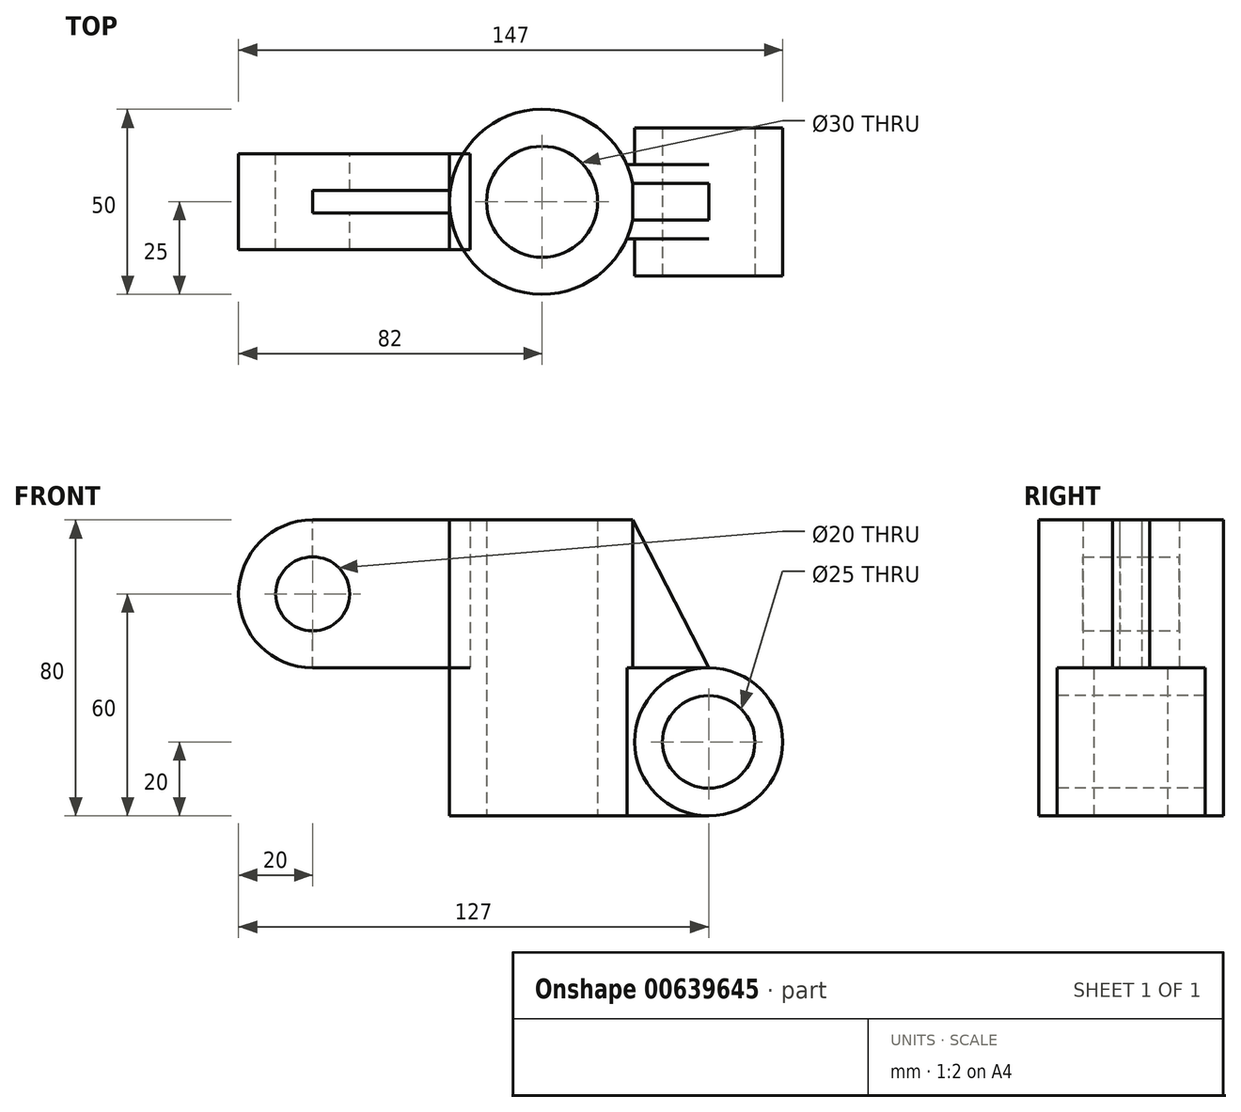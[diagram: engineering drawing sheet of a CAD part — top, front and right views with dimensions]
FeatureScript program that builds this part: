
annotation { "Feature Type Name" : "Feature", "Feature Type Description" : "" }
export const myFeature = defineFeature(function(context is Context, id is Id, definition is map)
    precondition{}
    {
        {
            var Q0;
            Q0=qCreatedBy(makeId("Top.planeOp"),FACE);
            var sketch = newSketch(context, id + "F0", { "sketchPlane" : qUnion([Q0])});
            skCircle(sketch, "E0", {"center": v(0, 0) * mm, "radius": 25 * mm});
            skCircle(sketch, "E1", {"center": v(0, 0) * mm, "radius": 15 * mm});
            skSolve(sketch);
        }
        {
            var Q0;
            Q0 = qSketchRegion(id + "F0", true);
            extrude(context, id + "F1", {"entities" : qUnion([Q0]), "depth" : 80 * mm, "offsetDistance" : 25 * mm});
        }
        {
            var Q0;
            Q0=qCreatedBy(makeId("Right.planeOp"),FACE);
            var sketch = newSketch(context, id + "F2", { "sketchPlane" : qUnion([Q0])});
            skLineSegment(sketch, "E2", {"start": v(-25, 0) * mm, "end": v(-25, 80) * mm});
            skLineSegment(sketch, "E3", {"start": v(25, 80) * mm, "end": v(25, 0) * mm});
            skLineSegment(sketch, "E4.0.0", {"start": v(-25, 80) * mm, "end": v(25, 80) * mm});
            skSolve(sketch);
        }
        {
            var Q0;
            Q0=makeQuery(id+"F1.opExtrude","CAP_FACE",FACE,{"disambiguationData":[OSD([sQuery(id+"F0.wireOp",EDGE,"E0"),sQuery(id+"F0.wireOp",EDGE,"E1")])],"isStart":false});
            var sketch = newSketch(context, id + "F3", { "sketchPlane" : qUnion([Q0])});
            skCircle(sketch, "E5.0", {"center": v(0, 0) * mm, "radius": 25 * mm});
            skPoint(sketch, "E6.0", {"position": v(0, 25) * mm});
            skLineSegment(sketch, "E7", {"start": v(0, 25) * mm, "end": v(45, 25) * mm});
            skLineSegment(sketch, "E8", {"start": v(45, 25) * mm, "end": v(45, -51.18) * mm});
            skLineSegment(sketch, "E9", {"start": v(0, 0) * mm, "end": v(45, 0) * mm});
            skLineSegment(sketch, "E10", {"start": v(45, 0) * mm, "end": v(45, 5) * mm});
            skLineSegment(sketch, "E11", {"start": v(45, 5) * mm, "end": v(45, -5) * mm});
            skLineSegment(sketch, "E12", {"start": v(45, -5) * mm, "end": v(0, -5) * mm});
            skLineSegment(sketch, "E13", {"start": v(0, -5) * mm, "end": v(0, 0) * mm});
            skLineSegment(sketch, "E14", {"start": v(0, 0) * mm, "end": v(0, 5) * mm});
            skLineSegment(sketch, "E15", {"start": v(0, 5) * mm, "end": v(45, 5) * mm});
            skSolve(sketch);
        }
        {
            var Q0;
            {var subQ0=sQuery(id+"F3.wireOp",EDGE,"E15");var subQ1=sQuery(id+"F3.wireOp",EDGE,"E5.0");var subQ2=makeQuery(id+"F3.imprint","INTERSECT",VERTEX,{"derivedFrom":[subQ1,subQ0]});Q0=makeQuery(id+"F3.imprint","IMPRINT",FACE,{"disambiguationData":[TD([[makeQuery(id+"F3.imprint","IMPRINT",EDGE,{"disambiguationData":[TD([[subQ2,1.0]])],"derivedFrom":subQ1}),-1.0]])]});}
            var Q1;
            {var subQ0=sQuery(id+"F3.wireOp",EDGE,"E12");var subQ1=sQuery(id+"F3.wireOp",EDGE,"E5.0");var subQ2=makeQuery(id+"F3.imprint","INTERSECT",VERTEX,{"derivedFrom":[subQ1,subQ0]});Q1=makeQuery(id+"F3.imprint","IMPRINT",FACE,{"disambiguationData":[TD([[makeQuery(id+"F3.imprint","IMPRINT",EDGE,{"disambiguationData":[TD([[subQ2,-1.0]])],"derivedFrom":subQ1}),-1.0]])]});}
            extrude(context, id + "F4", {"entities" : qUnion([Q0, Q1]), "operationType" : NewBodyOperationType.ADD, "oppositeDirection" : true, "depth" : 40 * mm, "offsetDistance" : 25 * mm});
        }
        {
            var Q0;
            Q0=makeQuery(id+"F4.opExtrude","SWEPT_FACE",FACE,{"disambiguationData":[OSD([sQuery(id+"F3.wireOp",EDGE,"E12")])]});
            var sketch = newSketch(context, id + "F5", { "sketchPlane" : qUnion([Q0])});
            skLineSegment(sketch, "E16", {"start": v(24.5, 80) * mm, "end": v(45, 40) * mm});
            skSolve(sketch);
        }
        {
            var Q0;
            Q0=makeQuery(id+"F5.imprint","IMPRINT",FACE,{"disambiguationData":[TD([[makeQuery(id+"F5.imprint","IMPRINT",EDGE,{"derivedFrom":sQuery(id+"F5.wireOp",EDGE,"E16")}),1.0]])]});
            extrude(context, id + "F6", {"entities" : qUnion([Q0]), "operationType" : NewBodyOperationType.REMOVE, "oppositeDirection" : true, "depth" : 25 * mm, "offsetDistance" : 25 * mm});
        }
        {
            var Q0;
            Q0=qCreatedBy(makeId("Top.planeOp"),FACE);
            var sketch = newSketch(context, id + "F7", { "sketchPlane" : qUnion([Q0])});
            skPoint(sketch, "E17.0", {"position": v(0, 0) * mm});
            skCircle(sketch, "E18.0", {"center": v(0, 0) * mm, "radius": 15 * mm});
            skCircle(sketch, "E19.0", {"center": v(0, 0) * mm, "radius": 25 * mm});
            skLineSegment(sketch, "E20", {"start": v(0, 25) * mm, "end": v(57, 25) * mm});
            skLineSegment(sketch, "E21", {"start": v(0, -25) * mm, "end": v(57, -25) * mm});
            skLineSegment(sketch, "E22", {"start": v(57, -25) * mm, "end": v(57, 25) * mm});
            skSolve(sketch);
        }
        {
            var Q0;
            Q0 = qSketchRegion(id + "F7", true);
            extrude(context, id + "F8", {"entities" : qUnion([Q0]), "operationType" : NewBodyOperationType.ADD, "depth" : 40 * mm, "offsetDistance" : 25 * mm});
        }
        {
            var Q0;
            Q0=makeQuery(id+"F8.opExtrude","CAP_FACE",FACE,{"disambiguationData":[OSD([sQuery(id+"F7.wireOp",EDGE,"E18.0"),sQuery(id+"F7.wireOp",EDGE,"E19.0"),sQuery(id+"F7.wireOp",EDGE,"E20"),sQuery(id+"F7.wireOp",EDGE,"E21"),sQuery(id+"F7.wireOp",EDGE,"E22")])],"isStart":false});
            var sketch = newSketch(context, id + "F9", { "sketchPlane" : qUnion([Q0])});
            skLineSegment(sketch, "E23", {"start": v(45, 0) * mm, "end": v(45, -10) * mm});
            skLineSegment(sketch, "E24", {"start": v(45, -10) * mm, "end": v(45, 10) * mm});
            skLineSegment(sketch, "E25", {"start": v(45, 10) * mm, "end": v(24.5, 10) * mm});
            skLineSegment(sketch, "E26", {"start": v(24.5, 10) * mm, "end": v(22.91, 10) * mm});
            skLineSegment(sketch, "E27", {"start": v(45, -10) * mm, "end": v(22.91, -10) * mm});
            skSolve(sketch);
        }
        {
            var Q0;
            {var subQ13=sQuery(id+"F9.wireOp",EDGE,"E25");Q0=makeQuery(id+"F9.imprint","IMPRINT",FACE,{"disambiguationData":[TD([[makeQuery(id+"F9.imprint","IMPRINT",EDGE,{"derivedFrom":subQ13}),-1.0]])]});}
            extrude(context, id + "F10", {"entities" : qUnion([Q0]), "operationType" : NewBodyOperationType.REMOVE, "oppositeDirection" : true, "depth" : 49.5 * mm, "offsetDistance" : 25 * mm});
        }
        {
            var Q0;
            Q0=makeQuery(id+"F10.boolean.opBoolean","COPY",FACE,{"derivedFrom":makeQuery(id+"F10.opExtrude","SWEPT_FACE",FACE,{"disambiguationData":[OSD([sQuery(id+"F9.wireOp",EDGE,"E25"),sQuery(id+"F9.wireOp",EDGE,"E26")])]})});
            var sketch = newSketch(context, id + "F11", { "sketchPlane" : qUnion([Q0])});
            skCircle(sketch, "E28", {"center": v(-45, 20) * mm, "radius": 20 * mm});
            skCircle(sketch, "E29", {"center": v(-45, 20) * mm, "radius": 12.5 * mm});
            skSolve(sketch);
        }
        {
            var Q0;
            {var subQ2=sQuery(id+"F9.wireOp",EDGE,"E25");var subQ3=makeQuery(id+"F10.boolean.opBoolean","COPY",EDGE,{"derivedFrom":makeQuery(id+"F10.opExtrude","SWEPT_EDGE",EDGE,{"disambiguationData":[OSD([sQuery(id+"F9.wireOp",EDGE,"E24"),subQ2])]})});var subQ6=sQuery(id+"F11.wireOp",EDGE,"E29");var subQ7=makeQuery(id+"F11.imprint","INTERSECT",VERTEX,{"disambiguationData":[OD(0.0)],"derivedFrom":[subQ3,subQ6]});Q0=makeQuery(id+"F11.imprint","IMPRINT",FACE,{"disambiguationData":[TD([[makeQuery(id+"F11.imprint","IMPRINT",EDGE,{"disambiguationData":[TD([[subQ7,1.0]])],"derivedFrom":subQ6}),-1.0]])]});}
            var Q1;
            {var subQ2=sQuery(id+"F9.wireOp",EDGE,"E25");var subQ3=makeQuery(id+"F10.boolean.opBoolean","COPY",EDGE,{"derivedFrom":makeQuery(id+"F10.opExtrude","SWEPT_EDGE",EDGE,{"disambiguationData":[OSD([sQuery(id+"F9.wireOp",EDGE,"E24"),subQ2])]})});var subQ6=sQuery(id+"F11.wireOp",EDGE,"E29");var subQ7=makeQuery(id+"F11.imprint","INTERSECT",VERTEX,{"disambiguationData":[OD(0.0)],"derivedFrom":[subQ3,subQ6]});Q1=makeQuery(id+"F11.imprint","IMPRINT",FACE,{"disambiguationData":[TD([[makeQuery(id+"F11.imprint","IMPRINT",EDGE,{"disambiguationData":[TD([[subQ7,-1.0]])],"derivedFrom":subQ6}),-1.0]])]});}
            extrude(context, id + "F12", {"entities" : qUnion([Q0, Q1]), "operationType" : NewBodyOperationType.ADD, "depth" : 10 * mm, "offsetDistance" : 25 * mm, "hasSecondDirection" : true, "secondDirectionOppositeDirection" : true, "secondDirectionDepth" : 30 * mm});
        }
        {
            var Q0;
            Q0=makeQuery(id+"F12.boolean.opBoolean","SPLIT",FACE,{"disambiguationData":[TD([makeQuery(id+"F10.boolean.opBoolean","COPY",FACE,{"derivedFrom":makeQuery(id+"F10.opExtrude","SWEPT_FACE",FACE,{"disambiguationData":[OSD([sQuery(id+"F9.wireOp",EDGE,"E24")])]})})])],"derivedFrom":makeQuery(id+"F10.boolean.opBoolean","COPY",FACE,{"derivedFrom":makeQuery(id+"F10.opExtrude","SWEPT_FACE",FACE,{"disambiguationData":[OSD([sQuery(id+"F9.wireOp",EDGE,"E25"),sQuery(id+"F9.wireOp",EDGE,"E26")])]})})});
            extrude(context, id + "F13", {"entities" : qUnion([Q0]), "operationType" : NewBodyOperationType.REMOVE, "oppositeDirection" : true, "depth" : 25 * mm, "offsetDistance" : 25 * mm});
        }
        {
            var Q0;
            {var subQ1=sQuery(id+"F3.wireOp",EDGE,"E5.0");var subQ8=makeQuery(id+"F3.imprint","INTERSECT",VERTEX,{"derivedFrom":[subQ1,sQuery(id+"F3.wireOp",EDGE,"E7")]});Q0=makeQuery(id+"F3.imprint","IMPRINT",FACE,{"disambiguationData":[TD([[makeQuery(id+"F3.imprint","IMPRINT",EDGE,{"disambiguationData":[TD([[subQ8,1.0]])],"derivedFrom":subQ1}),1.0]])]});}
            var sketch = newSketch(context, id + "F14", { "sketchPlane" : qUnion([Q0])});
            skArc(sketch, "E30.0.0", {"start": v(14.14, -5) * mm, "mid": v(-15, 0) * mm, "end": v(14.14, 5) * mm});
            skLineSegment(sketch, "E30.0.1", {"start": v(14.14, 5) * mm, "end": v(24.5, 5) * mm});
            skArc(sketch, "E30.0.2", {"start": v(24.5, 5) * mm, "mid": v(15.81, 19.36) * mm, "end": v(0, 25) * mm});
            skArc(sketch, "E30.0.3", {"start": v(0, 25) * mm, "mid": v(-19.36, -15.81) * mm, "end": v(24.5, -5) * mm});
            skLineSegment(sketch, "E30.0.4", {"start": v(24.5, -5) * mm, "end": v(14.14, -5) * mm});
            skLineSegment(sketch, "E31", {"start": v(0, -25) * mm, "end": v(-37, -25) * mm});
            skLineSegment(sketch, "E32", {"start": v(0, 25) * mm, "end": v(-37, 25) * mm});
            skLineSegment(sketch, "E33", {"start": v(-37, 25) * mm, "end": v(-37, -25) * mm});
            skSolve(sketch);
        }
        {
            var Q0;
            {var subQ1=sQuery(id+"F3.wireOp",EDGE,"E5.0");var subQ8=makeQuery(id+"F3.imprint","INTERSECT",VERTEX,{"derivedFrom":[subQ1,sQuery(id+"F3.wireOp",EDGE,"E7")]});Q0=makeQuery(id+"F3.imprint","IMPRINT",FACE,{"disambiguationData":[TD([[makeQuery(id+"F3.imprint","IMPRINT",EDGE,{"disambiguationData":[TD([[subQ8,1.0]])],"derivedFrom":subQ1}),1.0]])]});}
            var sketch = newSketch(context, id + "F15", { "sketchPlane" : qUnion([Q0])});
            skArc(sketch, "E34.0.0", {"start": v(14.14, -5) * mm, "mid": v(-15, 0) * mm, "end": v(14.14, 5) * mm});
            skLineSegment(sketch, "E34.0.1", {"start": v(14.14, 5) * mm, "end": v(24.5, 5) * mm});
            skArc(sketch, "E34.0.2", {"start": v(24.5, 5) * mm, "mid": v(15.81, 19.36) * mm, "end": v(0, 25) * mm});
            skArc(sketch, "E34.0.3", {"start": v(0, 25) * mm, "mid": v(-25, 0) * mm, "end": v(0, -25) * mm});
            skArc(sketch, "E34.0.4", {"start": v(0, -25) * mm, "mid": v(15.81, -19.36) * mm, "end": v(24.5, -5) * mm});
            skLineSegment(sketch, "E34.0.5", {"start": v(24.5, -5) * mm, "end": v(14.14, -5) * mm});
            skLineSegment(sketch, "E35", {"start": v(-25, 0) * mm, "end": v(-62, 0) * mm});
            skSolve(sketch);
        }
        {
            var Q0;
            Q0=qCreatedBy(makeId("Front.planeOp"),FACE);
            var sketch = newSketch(context, id + "F16", { "sketchPlane" : qUnion([Q0])});
            skLineSegment(sketch, "E36.0", {"start": v(-25, 80) * mm, "end": v(-62, 80) * mm});
            skLineSegment(sketch, "E37", {"start": v(-62, 80) * mm, "end": v(-62, 40) * mm});
            skLineSegment(sketch, "E38", {"start": v(-62, 40) * mm, "end": v(-62, 60) * mm});
            skCircle(sketch, "E39", {"center": v(-62, 60) * mm, "radius": 10 * mm});
            skCircle(sketch, "E40", {"center": v(-62, 60) * mm, "radius": 20 * mm});
            skLineSegment(sketch, "E41", {"start": v(-62, 40) * mm, "end": v(-25, 40) * mm});
            skLineSegment(sketch, "E42", {"start": v(-25, 80) * mm, "end": v(-25, 40) * mm});
            skSolve(sketch);
        }
        {
            var Q0;
            Q0 = qSketchRegion(id + "F16", true);
            extrude(context, id + "F17", {"entities" : qUnion([Q0]), "operationType" : NewBodyOperationType.ADD, "depth" : 13 * mm, "offsetDistance" : 25 * mm, "hasSecondDirection" : true, "secondDirectionOppositeDirection" : true, "secondDirectionDepth" : 13 * mm});
        }
        {
            var Q0;
            Q0=makeQuery(id+"F17.opExtrude","SWEPT_FACE",FACE,{"disambiguationData":[OSD([sQuery(id+"F16.wireOp",EDGE,"E42")])]});
            var sketch = newSketch(context, id + "F18", { "sketchPlane" : qUnion([Q0])});
            skSolve(sketch);
        }
        {
            var Q0;
            {var subQ0=sQuery(id+"F16.wireOp",EDGE,"E42");Q0=makeQuery(id+"F18.imprint","IMPRINT",FACE,{"disambiguationData":[TD([[makeQuery(id+"F18.imprint","IMPRINT",EDGE,{"derivedFrom":makeQuery(id+"F17.opExtrude","CAP_EDGE",EDGE,{"disambiguationData":[OSD([subQ0])],"isStart":true})}),-1.0]])]});}
            extrude(context, id + "F19", {"entities" : qUnion([Q0]), "depth" : 5.5 * mm, "offsetDistance" : 25 * mm});
        }
        {
            var Q0;
            Q0=makeQuery(id+"F17.opExtrude","SWEPT_FACE",FACE,{"disambiguationData":[OSD([sQuery(id+"F16.wireOp",EDGE,"E36.0")])]});
            var sketch = newSketch(context, id + "F20", { "sketchPlane" : qUnion([Q0])});
            skArc(sketch, "E43.0", {"start": v(14.14, -5) * mm, "mid": v(-15, 0) * mm, "end": v(14.14, 5) * mm});
            skLineSegment(sketch, "E44.0.1", {"start": v(14.14, 5) * mm, "end": v(24.5, 5) * mm});
            skArc(sketch, "E44.0.2", {"start": v(24.5, 5) * mm, "mid": v(15.81, 19.36) * mm, "end": v(0, 25) * mm});
            skArc(sketch, "E44.0.3", {"start": v(0, 25) * mm, "mid": v(-25, 0) * mm, "end": v(0, -25) * mm});
            skArc(sketch, "E44.0.4", {"start": v(0, -25) * mm, "mid": v(15.81, -19.36) * mm, "end": v(24.5, -5) * mm});
            skLineSegment(sketch, "E44.0.5", {"start": v(24.5, -5) * mm, "end": v(14.14, -5) * mm});
            skLineSegment(sketch, "E45.0", {"start": v(-25, 0) * mm, "end": v(-62, 0) * mm});
            skLineSegment(sketch, "E46.0.0", {"start": v(-25, 13) * mm, "end": v(-62, 13) * mm});
            skLineSegment(sketch, "E46.0.1", {"start": v(-62, 13) * mm, "end": v(-62, -13) * mm});
            skLineSegment(sketch, "E46.0.2", {"start": v(-62, -13) * mm, "end": v(-25, -13) * mm});
            skLineSegment(sketch, "E46.0.3", {"start": v(-25, -13) * mm, "end": v(-25, 13) * mm});
            skLineSegment(sketch, "E47", {"start": v(-82, -13) * mm, "end": v(-82, 13) * mm});
            skLineSegment(sketch, "E48", {"start": v(-25, 0) * mm, "end": v(-25, 3) * mm});
            skLineSegment(sketch, "E49", {"start": v(-25, 3) * mm, "end": v(-25, -3) * mm});
            skLineSegment(sketch, "E50", {"start": v(-25, -3) * mm, "end": v(-82, -3) * mm});
            skLineSegment(sketch, "E51", {"start": v(-82, -3) * mm, "end": v(-82, 3) * mm});
            skLineSegment(sketch, "E52", {"start": v(-82, 3) * mm, "end": v(-25, 3) * mm});
            skSolve(sketch);
        }
        {
            var Q0;
            {var subQ0=sQuery(id+"F20.wireOp",EDGE,"E45.0");Q0=makeQuery(id+"F20.imprint","IMPRINT",FACE,{"disambiguationData":[TD([[makeQuery(id+"F20.imprint","IMPRINT",EDGE,{"derivedFrom":subQ0}),-1.0]])]});}
            var Q1;
            {var subQ0=sQuery(id+"F20.wireOp",EDGE,"E45.0");Q1=makeQuery(id+"F20.imprint","IMPRINT",FACE,{"disambiguationData":[TD([[makeQuery(id+"F20.imprint","IMPRINT",EDGE,{"derivedFrom":subQ0}),1.0]])]});}
            var Q2;
            {var subQ0=sQuery(id+"F20.wireOp",EDGE,"E51");Q2=makeQuery(id+"F20.imprint","IMPRINT",FACE,{"disambiguationData":[TD([[makeQuery(id+"F20.imprint","IMPRINT",EDGE,{"derivedFrom":subQ0}),-1.0]])]});}
            extrude(context, id + "F21", {"entities" : qUnion([Q0, Q1, Q2]), "operationType" : NewBodyOperationType.REMOVE, "oppositeDirection" : true, "depth" : 156.4 * mm, "offsetDistance" : 25 * mm});
        }
    });
